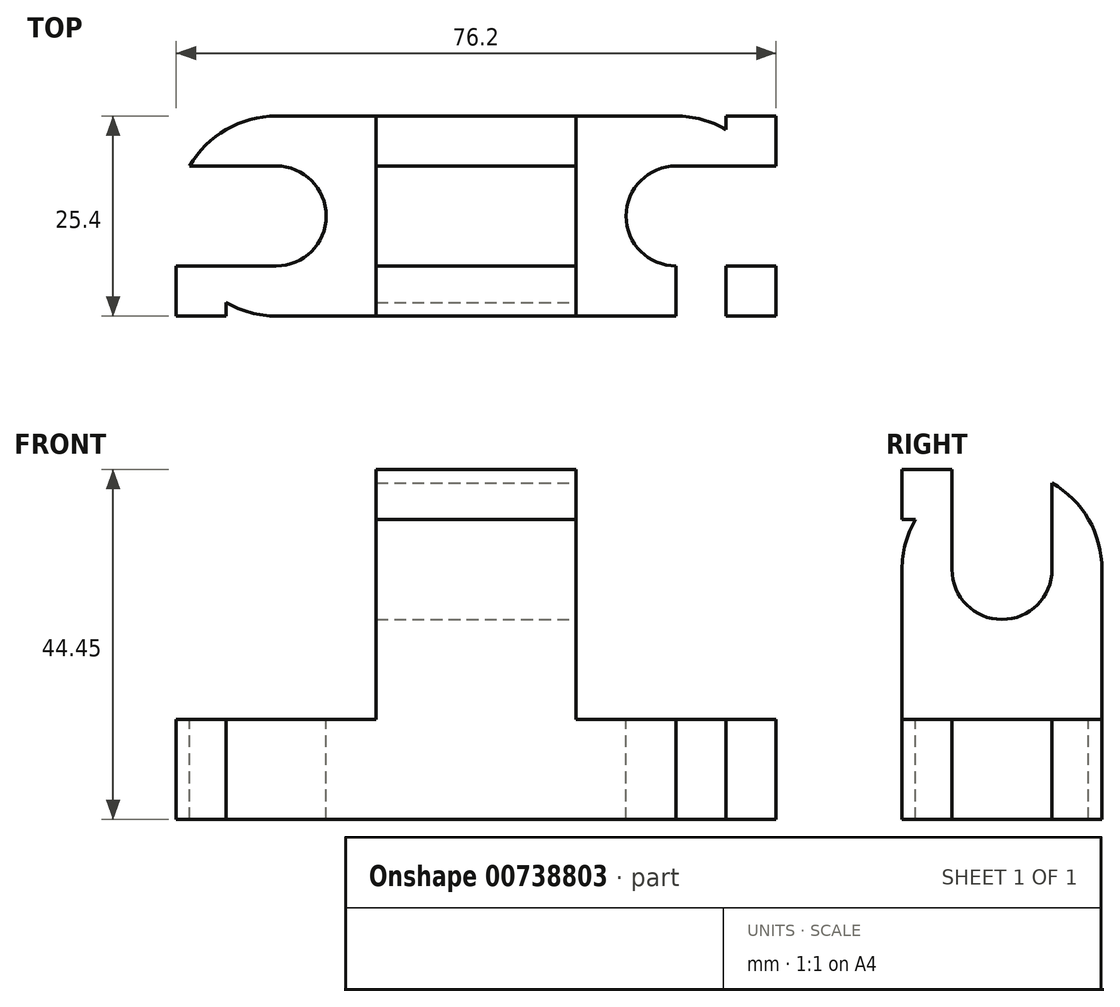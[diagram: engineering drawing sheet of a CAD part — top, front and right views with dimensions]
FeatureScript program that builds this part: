
annotation { "Feature Type Name" : "Feature", "Feature Type Description" : "" }
export const myFeature = defineFeature(function(context is Context, id is Id, definition is map)
    precondition{}
    {
        {
            var Q0;
            Q0=qCreatedBy(makeId("Front.planeOp"),FACE);
            var sketch = newSketch(context, id + "F0", { "sketchPlane" : qUnion([Q0])});
            skLineSegment(sketch, "E0.bottom", {"start": v(-41.12, 26.37) * mm, "end": v(35.08, 26.37) * mm});
            skLineSegment(sketch, "E0.top", {"start": v(-41.12, -18.08) * mm, "end": v(35.08, -18.08) * mm});
            skLineSegment(sketch, "E0.left", {"start": v(-41.12, 26.37) * mm, "end": v(-41.12, -18.08) * mm});
            skLineSegment(sketch, "E0.right", {"start": v(35.08, 26.37) * mm, "end": v(35.08, -18.08) * mm});
            skSolve(sketch);
        }
        {
            var Q0;
            Q0 = qSketchRegion(id + "F0", true);
            extrude(context, id + "F1", {"entities" : qUnion([Q0]), "depth" : 25.4 * mm, "offsetDistance" : 25.4 * mm});
        }
        {
            var Q0;
            Q0=makeQuery(id+"F1.opExtrude","CAP_FACE",FACE,{"disambiguationData":[OSD([sQuery(id+"F0.wireOp",EDGE,"E0.bottom"),sQuery(id+"F0.wireOp",EDGE,"E0.top"),sQuery(id+"F0.wireOp",EDGE,"E0.left"),sQuery(id+"F0.wireOp",EDGE,"E0.right")])],"isStart":false});
            var sketch = newSketch(context, id + "F2", { "sketchPlane" : qUnion([Q0])});
            skLineSegment(sketch, "E1", {"start": v(-15.72, 26.37) * mm, "end": v(-15.72, -5.38) * mm});
            skLineSegment(sketch, "E2", {"start": v(-15.72, -5.38) * mm, "end": v(-41.12, -5.38) * mm});
            skLineSegment(sketch, "E3", {"start": v(9.68, 26.37) * mm, "end": v(9.68, -5.38) * mm});
            skLineSegment(sketch, "E4", {"start": v(9.68, -5.38) * mm, "end": v(35.08, -5.38) * mm});
            skSolve(sketch);
        }
        {
            var Q0;
            Q0 = qSketchRegion(id + "F2", true);
            var Q1;
            {var subQ0=sQuery(id+"F2.wireOp",EDGE,"E1");Q1=makeQuery(id+"F2.imprint","IMPRINT",FACE,{"disambiguationData":[TD([[makeQuery(id+"F2.imprint","IMPRINT",EDGE,{"derivedFrom":subQ0}),-1.0]])]});}
            var Q2;
            {var subQ0=sQuery(id+"F2.wireOp",EDGE,"E3");Q2=makeQuery(id+"F2.imprint","IMPRINT",FACE,{"disambiguationData":[TD([[makeQuery(id+"F2.imprint","IMPRINT",EDGE,{"derivedFrom":subQ0}),1.0]])]});}
            extrude(context, id + "F3", {"entities" : qUnion([Q0, Q1, Q2]), "operationType" : NewBodyOperationType.REMOVE, "endBound" : BoundingType.THROUGH_ALL, "oppositeDirection" : true, "depth" : 25.4 * mm, "offsetDistance" : 25.4 * mm});
        }
        {
            var Q0;
            Q0=makeQuery(id+"F3.boolean.opBoolean","COPY",FACE,{"derivedFrom":makeQuery(id+"F3.opExtrude","SWEPT_FACE",FACE,{"disambiguationData":[OSD([sQuery(id+"F2.wireOp",EDGE,"E3")])]})});
            var sketch = newSketch(context, id + "F4", { "sketchPlane" : qUnion([Q0])});
            skLineSegment(sketch, "E5", {"start": v(-25.4, 20.02) * mm, "end": v(0, 20.02) * mm});
            skLineSegment(sketch, "E6", {"start": v(-25.4, 7.32) * mm, "end": v(0, 7.32) * mm});
            skLineSegment(sketch, "E7", {"start": v(-19.05, -5.38) * mm, "end": v(-19.05, 26.37) * mm});
            skLineSegment(sketch, "E8", {"start": v(-6.35, -5.38) * mm, "end": v(-6.35, 26.37) * mm});
            skCircle(sketch, "E9", {"center": v(-12.7, 13.67) * mm, "radius": 6.35 * mm});
            skLineSegment(sketch, "E10", {"start": v(-25.4, 13.67) * mm, "end": v(0, 13.67) * mm});
            skPoint(sketch, "E10.startSnap0", {"position": v(-25.4, 10.5) * mm});
            skArc(sketch, "E11", {"start": v(0, 13.67) * mm, "mid": v(-12.7, 26.37) * mm, "end": v(-25.4, 13.67) * mm});
            skSolve(sketch);
        }
        {
            var Q0;
            {var subQ0=sQuery(id+"F4.wireOp",EDGE,"E9");var subQ1=makeQuery(id+"F4.imprint","INTERSECT",VERTEX,{"derivedFrom":[sQuery(id+"F4.wireOp",EDGE,"E5"),subQ0]});Q0=makeQuery(id+"F4.imprint","IMPRINT",FACE,{"disambiguationData":[TD([[makeQuery(id+"F4.imprint","IMPRINT",EDGE,{"disambiguationData":[TD([[subQ1,1.0]])],"derivedFrom":subQ0}),1.0]])]});}
            var Q1;
            {var subQ0=sQuery(id+"F4.wireOp",EDGE,"E9");var subQ1=makeQuery(id+"F4.imprint","INTERSECT",VERTEX,{"derivedFrom":[sQuery(id+"F4.wireOp",EDGE,"E6"),subQ0]});Q1=makeQuery(id+"F4.imprint","IMPRINT",FACE,{"disambiguationData":[TD([[makeQuery(id+"F4.imprint","IMPRINT",EDGE,{"disambiguationData":[TD([[subQ1,1.0]])],"derivedFrom":subQ0}),1.0]])]});}
            var Q2;
            {var subQ0=sQuery(id+"F4.wireOp",EDGE,"E11");var subQ1=sQuery(id+"F4.wireOp",EDGE,"E5");var subQ2=makeQuery(id+"F4.imprint","INTERSECT",VERTEX,{"disambiguationData":[OD(1.0)],"derivedFrom":[subQ1,subQ0]});Q2=makeQuery(id+"F4.imprint","IMPRINT",FACE,{"disambiguationData":[TD([[makeQuery(id+"F4.imprint","IMPRINT",EDGE,{"disambiguationData":[TD([[subQ2,-1.0]])],"derivedFrom":subQ0}),-1.0]])]});}
            var Q3;
            {var subQ0=sQuery(id+"F2.wireOp",EDGE,"E3");var subQ1=makeQuery(id+"F3.boolean.opBoolean","COPY",EDGE,{"derivedFrom":makeQuery(id+"F3.opExtrude","CAP_EDGE",EDGE,{"disambiguationData":[OSD([subQ0])],"isStart":true})});var subQ6=sQuery(id+"F4.wireOp",EDGE,"E5");var subQ7=makeQuery(id+"F4.imprint","INTERSECT",VERTEX,{"derivedFrom":[subQ1,subQ6]});Q3=makeQuery(id+"F4.imprint","IMPRINT",FACE,{"disambiguationData":[TD([[makeQuery(id+"F4.imprint","IMPRINT",EDGE,{"disambiguationData":[TD([[subQ7,-1.0]])],"derivedFrom":subQ6}),1.0]])]});}
            var Q4;
            {var subQ0=sQuery(id+"F4.wireOp",EDGE,"E7");var subQ3=sQuery(id+"F4.wireOp",EDGE,"E11");var subQ4=makeQuery(id+"F4.imprint","INTERSECT",VERTEX,{"derivedFrom":[subQ0,subQ3]});Q4=makeQuery(id+"F4.imprint","IMPRINT",FACE,{"disambiguationData":[TD([[makeQuery(id+"F4.imprint","IMPRINT",EDGE,{"disambiguationData":[TD([[subQ4,-1.0]])],"derivedFrom":subQ0}),-1.0]])]});}
            var Q5;
            {var subQ0=sQuery(id+"F4.wireOp",EDGE,"E8");var subQ3=sQuery(id+"F4.wireOp",EDGE,"E11");var subQ4=makeQuery(id+"F4.imprint","INTERSECT",VERTEX,{"derivedFrom":[subQ0,subQ3]});Q5=makeQuery(id+"F4.imprint","IMPRINT",FACE,{"disambiguationData":[TD([[makeQuery(id+"F4.imprint","IMPRINT",EDGE,{"disambiguationData":[TD([[subQ4,-1.0]])],"derivedFrom":subQ0}),1.0]])]});}
            var Q6;
            {var subQ0=sQuery(id+"F4.wireOp",EDGE,"E5");var subQ1=makeQuery(id+"F3.boolean.opBoolean","COPY",EDGE,{"derivedFrom":makeQuery(id+"F3.opExtrude","CAP_EDGE",EDGE,{"disambiguationData":[OSD([sQuery(id+"F2.wireOp",EDGE,"E3")])],"isStart":true})});var subQ2=makeQuery(id+"F4.imprint","INTERSECT",VERTEX,{"derivedFrom":[subQ1,subQ0]});Q6=makeQuery(id+"F4.imprint","IMPRINT",FACE,{"disambiguationData":[TD([[makeQuery(id+"F4.imprint","IMPRINT",EDGE,{"disambiguationData":[TD([[subQ2,-1.0]])],"derivedFrom":subQ0}),-1.0]])]});}
            var Q7;
            {var subQ0=sQuery(id+"F4.wireOp",EDGE,"E5");var subQ3=sQuery(id+"F4.wireOp",EDGE,"E11");var subQ4=makeQuery(id+"F4.imprint","INTERSECT",VERTEX,{"disambiguationData":[OD(1.0)],"derivedFrom":[subQ0,subQ3]});Q7=makeQuery(id+"F4.imprint","IMPRINT",FACE,{"disambiguationData":[TD([[makeQuery(id+"F4.imprint","IMPRINT",EDGE,{"disambiguationData":[TD([[subQ4,-1.0]])],"derivedFrom":subQ0}),-1.0]])]});}
            extrude(context, id + "F5", {"entities" : qUnion([Q0, Q1, Q2, Q3, Q4, Q5, Q6, Q7]), "operationType" : NewBodyOperationType.REMOVE, "endBound" : BoundingType.THROUGH_ALL, "oppositeDirection" : true, "depth" : 25.4 * mm, "offsetDistance" : 25.4 * mm});
        }
        {
            var Q0;
            Q0=makeQuery(id+"F3.boolean.opBoolean","COPY",FACE,{"derivedFrom":makeQuery(id+"F3.opExtrude","SWEPT_FACE",FACE,{"disambiguationData":[OSD([sQuery(id+"F2.wireOp",EDGE,"E2")])]})});
            var sketch = newSketch(context, id + "F6", { "sketchPlane" : qUnion([Q0])});
            skLineSegment(sketch, "E12", {"start": v(-34.77, 0) * mm, "end": v(-34.77, -25.4) * mm});
            skLineSegment(sketch, "E13", {"start": v(-22.07, 0) * mm, "end": v(-22.07, -25.4) * mm});
            skLineSegment(sketch, "E14", {"start": v(-41.12, -6.35) * mm, "end": v(-15.72, -6.35) * mm});
            skLineSegment(sketch, "E15", {"start": v(-41.12, -19.05) * mm, "end": v(-15.72, -19.05) * mm});
            skCircle(sketch, "E16", {"center": v(-28.42, -12.7) * mm, "radius": 6.35 * mm});
            skLineSegment(sketch, "E17", {"start": v(-28.42, 0) * mm, "end": v(-28.42, -25.4) * mm});
            skArc(sketch, "E18", {"start": v(-28.42, 0) * mm, "mid": v(-41.12, -12.7) * mm, "end": v(-28.42, -25.4) * mm});
            skSolve(sketch);
        }
        {
            var Q0;
            {var subQ0=sQuery(id+"F6.wireOp",EDGE,"E16");var subQ1=makeQuery(id+"F6.imprint","INTERSECT",VERTEX,{"derivedFrom":[sQuery(id+"F6.wireOp",EDGE,"E13"),subQ0]});Q0=makeQuery(id+"F6.imprint","IMPRINT",FACE,{"disambiguationData":[TD([[makeQuery(id+"F6.imprint","IMPRINT",EDGE,{"disambiguationData":[TD([[subQ1,-1.0]])],"derivedFrom":subQ0}),1.0]])]});}
            var Q1;
            {var subQ0=sQuery(id+"F6.wireOp",EDGE,"E16");var subQ1=makeQuery(id+"F6.imprint","INTERSECT",VERTEX,{"derivedFrom":[sQuery(id+"F6.wireOp",EDGE,"E12"),subQ0]});Q1=makeQuery(id+"F6.imprint","IMPRINT",FACE,{"disambiguationData":[TD([[makeQuery(id+"F6.imprint","IMPRINT",EDGE,{"disambiguationData":[TD([[subQ1,1.0]])],"derivedFrom":subQ0}),1.0]])]});}
            var Q2;
            {var subQ7=sQuery(id+"F6.wireOp",EDGE,"E18");var subQ8=sQuery(id+"F6.wireOp",EDGE,"E12");var subQ9=makeQuery(id+"F6.imprint","INTERSECT",VERTEX,{"disambiguationData":[OD(0.0)],"derivedFrom":[subQ8,subQ7]});Q2=makeQuery(id+"F6.imprint","IMPRINT",FACE,{"disambiguationData":[TD([[makeQuery(id+"F6.imprint","IMPRINT",EDGE,{"disambiguationData":[TD([[subQ9,-1.0]])],"derivedFrom":subQ7}),-1.0]])]});}
            var Q3;
            {var subQ0=sQuery(id+"F6.wireOp",EDGE,"E14");var subQ3=sQuery(id+"F6.wireOp",EDGE,"E18");var subQ4=makeQuery(id+"F6.imprint","INTERSECT",VERTEX,{"derivedFrom":[subQ0,subQ3]});Q3=makeQuery(id+"F6.imprint","IMPRINT",FACE,{"disambiguationData":[TD([[makeQuery(id+"F6.imprint","IMPRINT",EDGE,{"disambiguationData":[TD([[subQ4,1.0]])],"derivedFrom":subQ0}),-1.0]])]});}
            var Q4;
            {var subQ0=sQuery(id+"F6.wireOp",EDGE,"E12");var subQ3=sQuery(id+"F6.wireOp",EDGE,"E18");var subQ4=makeQuery(id+"F6.imprint","INTERSECT",VERTEX,{"disambiguationData":[OD(0.0)],"derivedFrom":[subQ0,subQ3]});Q4=makeQuery(id+"F6.imprint","IMPRINT",FACE,{"disambiguationData":[TD([[makeQuery(id+"F6.imprint","IMPRINT",EDGE,{"disambiguationData":[TD([[subQ4,1.0]])],"derivedFrom":subQ0}),1.0]])]});}
            var Q5;
            {var subQ0=sQuery(id+"F6.wireOp",EDGE,"E15");var subQ3=sQuery(id+"F6.wireOp",EDGE,"E18");var subQ4=makeQuery(id+"F6.imprint","INTERSECT",VERTEX,{"derivedFrom":[subQ0,subQ3]});Q5=makeQuery(id+"F6.imprint","IMPRINT",FACE,{"disambiguationData":[TD([[makeQuery(id+"F6.imprint","IMPRINT",EDGE,{"disambiguationData":[TD([[subQ4,1.0]])],"derivedFrom":subQ0}),1.0]])]});}
            var Q6;
            {var subQ0=sQuery(id+"F2.wireOp",EDGE,"E2");var subQ1=makeQuery(id+"F3.boolean.opBoolean","COPY",EDGE,{"derivedFrom":makeQuery(id+"F3.opExtrude","CAP_EDGE",EDGE,{"disambiguationData":[OSD([subQ0])],"isStart":true})});var subQ7=sQuery(id+"F6.wireOp",EDGE,"E12");var subQ10=makeQuery(id+"F6.imprint","INTERSECT",VERTEX,{"derivedFrom":[subQ1,subQ7]});Q6=makeQuery(id+"F6.imprint","IMPRINT",FACE,{"disambiguationData":[TD([[makeQuery(id+"F6.imprint","IMPRINT",EDGE,{"disambiguationData":[TD([[subQ10,1.0]])],"derivedFrom":subQ7}),-1.0]])]});}
            var Q7;
            {var subQ0=sQuery(id+"F6.wireOp",EDGE,"E12");var subQ1=makeQuery(id+"F3.boolean.opBoolean","COPY",EDGE,{"derivedFrom":makeQuery(id+"F3.opExtrude","CAP_EDGE",EDGE,{"disambiguationData":[OSD([sQuery(id+"F2.wireOp",EDGE,"E2")])],"isStart":true})});var subQ2=makeQuery(id+"F6.imprint","INTERSECT",VERTEX,{"derivedFrom":[subQ1,subQ0]});Q7=makeQuery(id+"F6.imprint","IMPRINT",FACE,{"disambiguationData":[TD([[makeQuery(id+"F6.imprint","IMPRINT",EDGE,{"disambiguationData":[TD([[subQ2,1.0]])],"derivedFrom":subQ0}),1.0]])]});}
            extrude(context, id + "F7", {"entities" : qUnion([Q0, Q1, Q2, Q3, Q4, Q5, Q6, Q7]), "operationType" : NewBodyOperationType.REMOVE, "endBound" : BoundingType.THROUGH_ALL, "oppositeDirection" : true, "depth" : 25.4 * mm, "offsetDistance" : 25.4 * mm});
        }
        {
            var Q0;
            Q0=makeQuery(id+"F3.boolean.opBoolean","COPY",FACE,{"derivedFrom":makeQuery(id+"F3.opExtrude","SWEPT_FACE",FACE,{"disambiguationData":[OSD([sQuery(id+"F2.wireOp",EDGE,"E4")])]})});
            var sketch = newSketch(context, id + "F8", { "sketchPlane" : qUnion([Q0])});
            skLineSegment(sketch, "E19", {"start": v(16.03, 0) * mm, "end": v(16.03, -25.4) * mm});
            skLineSegment(sketch, "E20", {"start": v(28.73, 0) * mm, "end": v(28.73, -25.4) * mm});
            skLineSegment(sketch, "E21", {"start": v(9.68, -6.35) * mm, "end": v(35.08, -6.35) * mm});
            skLineSegment(sketch, "E22", {"start": v(9.68, -19.05) * mm, "end": v(35.08, -19.05) * mm});
            skCircle(sketch, "E23", {"center": v(22.38, -12.7) * mm, "radius": 6.35 * mm});
            skPoint(sketch, "E23.centerSnap0", {"position": v(28.73, -12.7) * mm});
            skLineSegment(sketch, "E24", {"start": v(22.38, 0) * mm, "end": v(22.38, -25.4) * mm});
            skArc(sketch, "E25", {"start": v(22.38, -25.4) * mm, "mid": v(35.08, -12.7) * mm, "end": v(22.38, 0) * mm});
            skSolve(sketch);
        }
        {
            var Q0;
            {var subQ0=sQuery(id+"F8.wireOp",EDGE,"E23");var subQ1=makeQuery(id+"F8.imprint","INTERSECT",VERTEX,{"derivedFrom":[sQuery(id+"F8.wireOp",EDGE,"E20"),subQ0]});Q0=makeQuery(id+"F8.imprint","IMPRINT",FACE,{"disambiguationData":[TD([[makeQuery(id+"F8.imprint","IMPRINT",EDGE,{"disambiguationData":[TD([[subQ1,-1.0]])],"derivedFrom":subQ0}),1.0]])]});}
            var Q1;
            {var subQ0=sQuery(id+"F8.wireOp",EDGE,"E23");var subQ1=makeQuery(id+"F8.imprint","INTERSECT",VERTEX,{"derivedFrom":[sQuery(id+"F8.wireOp",EDGE,"E19"),subQ0]});Q1=makeQuery(id+"F8.imprint","IMPRINT",FACE,{"disambiguationData":[TD([[makeQuery(id+"F8.imprint","IMPRINT",EDGE,{"disambiguationData":[TD([[subQ1,1.0]])],"derivedFrom":subQ0}),1.0]])]});}
            var Q2;
            {var subQ0=sQuery(id+"F8.wireOp",EDGE,"E20");var subQ1=makeQuery(id+"F3.boolean.opBoolean","COPY",EDGE,{"derivedFrom":makeQuery(id+"F3.opExtrude","CAP_EDGE",EDGE,{"disambiguationData":[OSD([sQuery(id+"F2.wireOp",EDGE,"E4")])],"isStart":true})});var subQ2=makeQuery(id+"F8.imprint","INTERSECT",VERTEX,{"derivedFrom":[subQ1,subQ0]});Q2=makeQuery(id+"F8.imprint","IMPRINT",FACE,{"disambiguationData":[TD([[makeQuery(id+"F8.imprint","IMPRINT",EDGE,{"disambiguationData":[TD([[subQ2,1.0]])],"derivedFrom":subQ0}),-1.0]])]});}
            var Q3;
            {var subQ0=sQuery(id+"F2.wireOp",EDGE,"E4");var subQ1=makeQuery(id+"F3.boolean.opBoolean","COPY",EDGE,{"derivedFrom":makeQuery(id+"F3.opExtrude","CAP_EDGE",EDGE,{"disambiguationData":[OSD([subQ0])],"isStart":true})});var subQ7=sQuery(id+"F8.wireOp",EDGE,"E20");var subQ10=makeQuery(id+"F8.imprint","INTERSECT",VERTEX,{"derivedFrom":[subQ1,subQ7]});Q3=makeQuery(id+"F8.imprint","IMPRINT",FACE,{"disambiguationData":[TD([[makeQuery(id+"F8.imprint","IMPRINT",EDGE,{"disambiguationData":[TD([[subQ10,1.0]])],"derivedFrom":subQ7}),1.0]])]});}
            var Q4;
            {var subQ0=sQuery(id+"F8.wireOp",EDGE,"E22");var subQ3=sQuery(id+"F8.wireOp",EDGE,"E25");var subQ4=makeQuery(id+"F8.imprint","INTERSECT",VERTEX,{"derivedFrom":[subQ0,subQ3]});Q4=makeQuery(id+"F8.imprint","IMPRINT",FACE,{"disambiguationData":[TD([[makeQuery(id+"F8.imprint","IMPRINT",EDGE,{"disambiguationData":[TD([[subQ4,-1.0]])],"derivedFrom":subQ0}),1.0]])]});}
            var Q5;
            {var subQ0=sQuery(id+"F8.wireOp",EDGE,"E21");var subQ3=sQuery(id+"F8.wireOp",EDGE,"E25");var subQ4=makeQuery(id+"F8.imprint","INTERSECT",VERTEX,{"derivedFrom":[subQ0,subQ3]});Q5=makeQuery(id+"F8.imprint","IMPRINT",FACE,{"disambiguationData":[TD([[makeQuery(id+"F8.imprint","IMPRINT",EDGE,{"disambiguationData":[TD([[subQ4,-1.0]])],"derivedFrom":subQ0}),-1.0]])]});}
            var Q6;
            {var subQ7=sQuery(id+"F8.wireOp",EDGE,"E20");var subQ9=sQuery(id+"F8.wireOp",EDGE,"E25");var subQ10=makeQuery(id+"F8.imprint","INTERSECT",VERTEX,{"disambiguationData":[OD(0.0)],"derivedFrom":[subQ7,subQ9]});Q6=makeQuery(id+"F8.imprint","IMPRINT",FACE,{"disambiguationData":[TD([[makeQuery(id+"F8.imprint","IMPRINT",EDGE,{"disambiguationData":[TD([[subQ10,1.0]])],"derivedFrom":subQ9}),-1.0]])]});}
            var Q7;
            {var subQ0=sQuery(id+"F8.wireOp",EDGE,"E20");var subQ3=sQuery(id+"F8.wireOp",EDGE,"E25");var subQ4=makeQuery(id+"F8.imprint","INTERSECT",VERTEX,{"disambiguationData":[OD(0.0)],"derivedFrom":[subQ0,subQ3]});Q7=makeQuery(id+"F8.imprint","IMPRINT",FACE,{"disambiguationData":[TD([[makeQuery(id+"F8.imprint","IMPRINT",EDGE,{"disambiguationData":[TD([[subQ4,1.0]])],"derivedFrom":subQ0}),-1.0]])]});}
            extrude(context, id + "F9", {"entities" : qUnion([Q0, Q1, Q2, Q3, Q4, Q5, Q6, Q7]), "operationType" : NewBodyOperationType.REMOVE, "endBound" : BoundingType.THROUGH_ALL, "oppositeDirection" : true, "depth" : 25.4 * mm, "offsetDistance" : 25.4 * mm});
        }
    });
